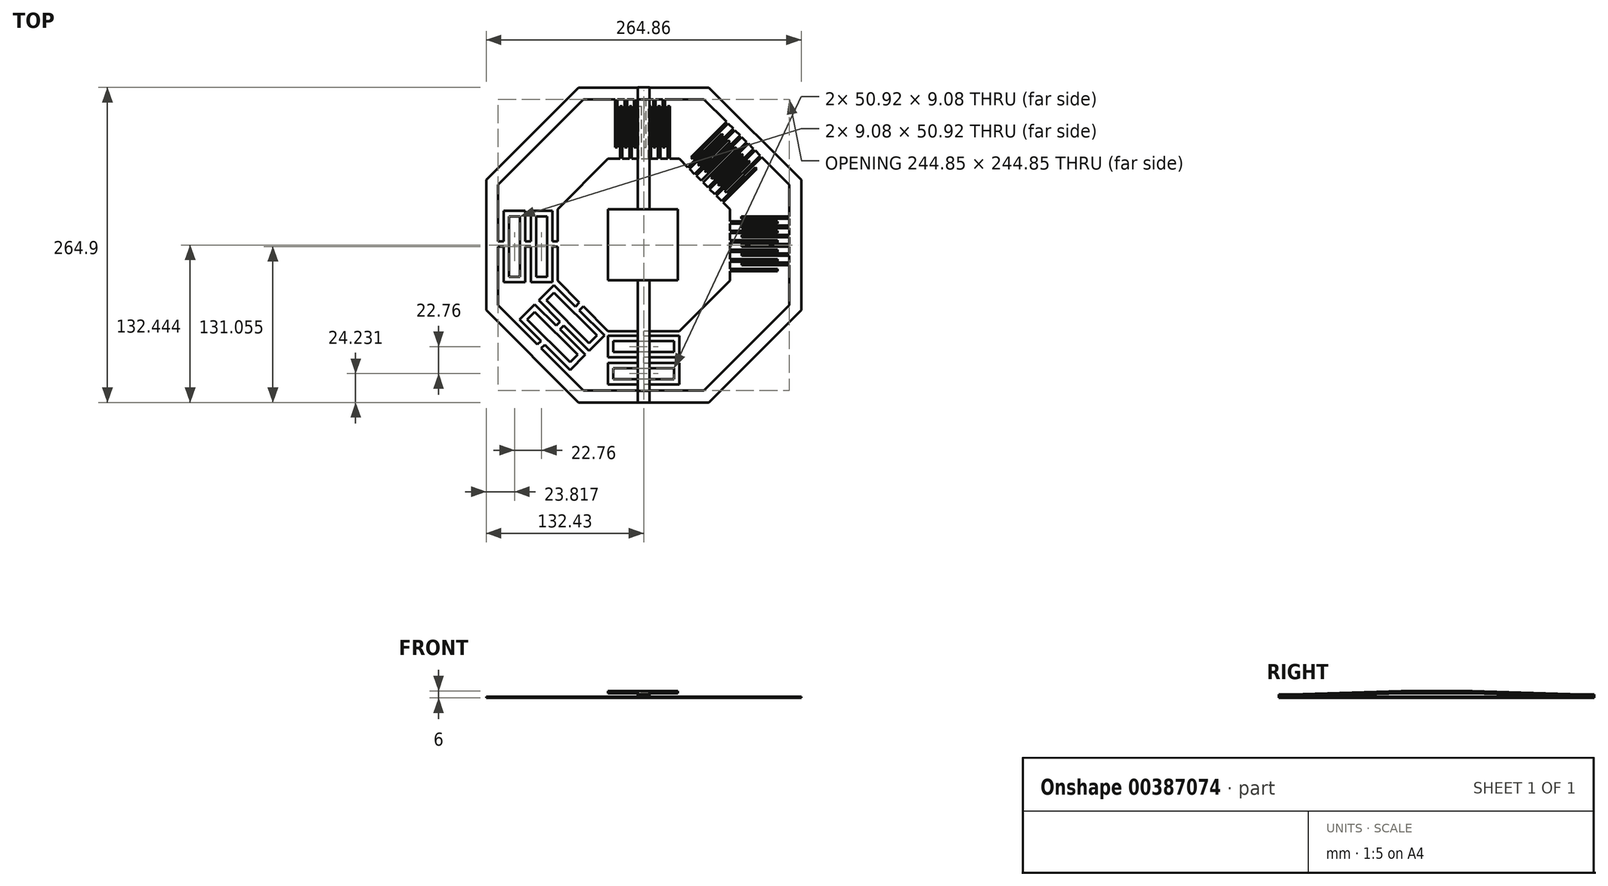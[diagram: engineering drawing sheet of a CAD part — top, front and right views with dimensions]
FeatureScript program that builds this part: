
annotation { "Feature Type Name" : "Feature", "Feature Type Description" : "" }
export const myFeature = defineFeature(function(context is Context, id is Id, definition is map)
    precondition{}
    {
        {
            var Q0;
            Q0=qCreatedBy(makeId("Top.planeOp"),FACE);
            var sketch = newSketch(context, id + "F0", { "sketchPlane" : qUnion([Q0])});
            skLineSegment(sketch, "E0", {"start": v(0, 0) * mm, "end": v(60, 0) * mm});
            skLineSegment(sketch, "E1", {"start": v(60, 0) * mm, "end": v(102.43, -42.43) * mm});
            skLineSegment(sketch, "E2", {"start": v(102.43, -42.43) * mm, "end": v(102.43, -52.43) * mm});
            skLineSegment(sketch, "E3", {"start": v(102.43, -102.43) * mm, "end": v(60, -144.85) * mm});
            skLineSegment(sketch, "E4", {"start": v(60, -144.85) * mm, "end": v(30, -144.85) * mm});
            skLineSegment(sketch, "E5", {"start": v(0, -144.85) * mm, "end": v(-20.84, -124.01) * mm});
            skLineSegment(sketch, "E6", {"start": v(-42.43, -102.43) * mm, "end": v(-42.43, -73.81) * mm});
            skLineSegment(sketch, "E7", {"start": v(-42.43, -42.43) * mm, "end": v(0, 0) * mm});
            skLineSegment(sketch, "E8.0", {"start": v(-92.43, -123.14) * mm, "end": v(-92.43, -73.81) * mm});
            skLineSegment(sketch, "E8.1", {"start": v(-20.71, -194.85) * mm, "end": v(-56.2, -159.37) * mm});
            skLineSegment(sketch, "E8.2", {"start": v(-92.43, -21.72) * mm, "end": v(-20.71, 50) * mm});
            skLineSegment(sketch, "E8.3", {"start": v(80.71, -194.85) * mm, "end": v(30, -194.85) * mm});
            skLineSegment(sketch, "E8.4", {"start": v(-20.71, 50) * mm, "end": v(6, 50) * mm});
            skLineSegment(sketch, "E8.6", {"start": v(152.43, -21.72) * mm, "end": v(152.43, -48.43) * mm});
            skLineSegment(sketch, "E8.7", {"start": v(152.43, -123.14) * mm, "end": v(80.71, -194.85) * mm});
            skLineSegment(sketch, "E9.0", {"start": v(-102.43, -17.57) * mm, "end": v(-24.85, 60) * mm});
            skLineSegment(sketch, "E9.1", {"start": v(-102.43, -127.28) * mm, "end": v(-102.43, -17.57) * mm});
            skLineSegment(sketch, "E9.2", {"start": v(-24.85, 60) * mm, "end": v(84.85, 60) * mm});
            skLineSegment(sketch, "E9.3", {"start": v(-24.85, -204.85) * mm, "end": v(-102.43, -127.28) * mm});
            skLineSegment(sketch, "E9.4", {"start": v(84.85, 60) * mm, "end": v(162.43, -17.57) * mm});
            skLineSegment(sketch, "E9.5", {"start": v(162.43, -17.57) * mm, "end": v(162.43, -127.28) * mm});
            skLineSegment(sketch, "E9.6", {"start": v(162.43, -127.28) * mm, "end": v(84.85, -204.85) * mm});
            skLineSegment(sketch, "E9.7", {"start": v(84.85, -204.85) * mm, "end": v(-24.85, -204.85) * mm});
            skLineSegment(sketch, "E10", {"start": v(10, 0) * mm, "end": v(10, 44.25) * mm});
            skLineSegment(sketch, "E11", {"start": v(10, 44.25) * mm, "end": v(12, 44.25) * mm});
            skLineSegment(sketch, "E12", {"start": v(12, 44.25) * mm, "end": v(12, 0) * mm});
            skLineSegment(sketch, "E13.1.0.0", {"start": v(20, 44.25) * mm, "end": v(20, 0) * mm});
            skLineSegment(sketch, "E13.1.0.1", {"start": v(18, 0) * mm, "end": v(18, 44.25) * mm});
            skLineSegment(sketch, "E13.1.0.2", {"start": v(18, 44.25) * mm, "end": v(20, 44.25) * mm});
            skLineSegment(sketch, "E13.2.0.0", {"start": v(28, 44.25) * mm, "end": v(28, 0) * mm});
            skLineSegment(sketch, "E13.2.0.1", {"start": v(26, 0) * mm, "end": v(26, 44.25) * mm});
            skLineSegment(sketch, "E13.2.0.2", {"start": v(26, 44.25) * mm, "end": v(28, 44.25) * mm});
            skLineSegment(sketch, "E13.3.0.0", {"start": v(36, 44.25) * mm, "end": v(36, 0) * mm});
            skLineSegment(sketch, "E13.3.0.1", {"start": v(34, 0) * mm, "end": v(34, 44.25) * mm});
            skLineSegment(sketch, "E13.3.0.2", {"start": v(34, 44.25) * mm, "end": v(36, 44.25) * mm});
            skLineSegment(sketch, "E13.4.0.0", {"start": v(44, 44.25) * mm, "end": v(44, 0) * mm});
            skLineSegment(sketch, "E13.4.0.1", {"start": v(42, 0) * mm, "end": v(42, 44.25) * mm});
            skLineSegment(sketch, "E13.4.0.2", {"start": v(42, 44.25) * mm, "end": v(44, 44.25) * mm});
            skLineSegment(sketch, "E13.5.0.0", {"start": v(52, 44.25) * mm, "end": v(52, 0) * mm});
            skLineSegment(sketch, "E13.5.0.1", {"start": v(50, 0) * mm, "end": v(50, 44.25) * mm});
            skLineSegment(sketch, "E13.5.0.2", {"start": v(50, 44.25) * mm, "end": v(52, 44.25) * mm});
            skLineSegment(sketch, "E13.direction1", {"start": v(10, 0) * mm, "end": v(18, 0) * mm, "construction": true});
            skLineSegment(sketch, "E14", {"start": v(102.43, -52.43) * mm, "end": v(142.43, -52.43) * mm});
            skLineSegment(sketch, "E15", {"start": v(142.43, -52.43) * mm, "end": v(142.43, -54.43) * mm});
            skLineSegment(sketch, "E16", {"start": v(142.43, -54.43) * mm, "end": v(102.43, -54.43) * mm});
            skLineSegment(sketch, "E17.1.0.0", {"start": v(102.43, -60.43) * mm, "end": v(142.43, -60.43) * mm});
            skLineSegment(sketch, "E17.1.0.1", {"start": v(142.43, -60.43) * mm, "end": v(142.43, -62.43) * mm});
            skLineSegment(sketch, "E17.1.0.2", {"start": v(142.43, -62.43) * mm, "end": v(102.43, -62.43) * mm});
            skLineSegment(sketch, "E17.2.0.0", {"start": v(102.43, -68.43) * mm, "end": v(142.43, -68.43) * mm});
            skLineSegment(sketch, "E17.2.0.1", {"start": v(142.43, -68.43) * mm, "end": v(142.43, -70.43) * mm});
            skLineSegment(sketch, "E17.2.0.2", {"start": v(142.43, -70.43) * mm, "end": v(102.43, -70.43) * mm});
            skLineSegment(sketch, "E17.3.0.0", {"start": v(102.43, -76.43) * mm, "end": v(142.43, -76.43) * mm});
            skLineSegment(sketch, "E17.3.0.1", {"start": v(142.43, -76.43) * mm, "end": v(142.43, -78.43) * mm});
            skLineSegment(sketch, "E17.3.0.2", {"start": v(142.43, -78.43) * mm, "end": v(102.43, -78.43) * mm});
            skLineSegment(sketch, "E17.4.0.0", {"start": v(102.43, -84.43) * mm, "end": v(142.43, -84.43) * mm});
            skLineSegment(sketch, "E17.4.0.1", {"start": v(142.43, -84.43) * mm, "end": v(142.43, -86.43) * mm});
            skLineSegment(sketch, "E17.4.0.2", {"start": v(142.43, -86.43) * mm, "end": v(102.43, -86.43) * mm});
            skLineSegment(sketch, "E17.5.0.0", {"start": v(102.43, -92.43) * mm, "end": v(142.43, -92.43) * mm});
            skLineSegment(sketch, "E17.5.0.1", {"start": v(142.43, -92.43) * mm, "end": v(142.43, -94.43) * mm});
            skLineSegment(sketch, "E17.5.0.2", {"start": v(142.43, -94.43) * mm, "end": v(102.43, -94.43) * mm});
            skLineSegment(sketch, "E17.direction1", {"start": v(102.43, -54.43) * mm, "end": v(102.43, -60.43) * mm, "construction": true});
            skLineSegment(sketch, "E18", {"start": v(80.71, 50) * mm, "end": v(99.6, 31.11) * mm});
            skLineSegment(sketch, "E19", {"start": v(67.07, -7.07) * mm, "end": v(95.36, 21.21) * mm});
            skLineSegment(sketch, "E20", {"start": v(95.36, 21.21) * mm, "end": v(96.77, 19.8) * mm});
            skLineSegment(sketch, "E21", {"start": v(96.77, 19.8) * mm, "end": v(68.49, -8.49) * mm});
            skLineSegment(sketch, "E22", {"start": v(68.49, -8.49) * mm, "end": v(67.07, -7.07) * mm});
            skLineSegment(sketch, "E23.1.0.0", {"start": v(72.73, -12.73) * mm, "end": v(101.01, 15.56) * mm});
            skLineSegment(sketch, "E23.1.0.1", {"start": v(102.43, 14.14) * mm, "end": v(74.14, -14.14) * mm});
            skLineSegment(sketch, "E23.1.0.2", {"start": v(101.01, 15.56) * mm, "end": v(102.43, 14.14) * mm});
            skLineSegment(sketch, "E23.1.0.3", {"start": v(74.14, -14.14) * mm, "end": v(72.73, -12.73) * mm});
            skLineSegment(sketch, "E23.2.0.0", {"start": v(78.38, -18.38) * mm, "end": v(106.67, 9.9) * mm});
            skLineSegment(sketch, "E23.2.0.1", {"start": v(108.08, 8.49) * mm, "end": v(79.8, -19.8) * mm});
            skLineSegment(sketch, "E23.2.0.2", {"start": v(106.67, 9.9) * mm, "end": v(108.08, 8.49) * mm});
            skLineSegment(sketch, "E23.2.0.3", {"start": v(79.8, -19.8) * mm, "end": v(78.38, -18.38) * mm});
            skLineSegment(sketch, "E23.3.0.0", {"start": v(84.04, -24.04) * mm, "end": v(112.33, 4.24) * mm});
            skLineSegment(sketch, "E23.3.0.1", {"start": v(113.74, 2.83) * mm, "end": v(85.46, -25.46) * mm});
            skLineSegment(sketch, "E23.3.0.2", {"start": v(112.33, 4.24) * mm, "end": v(113.74, 2.83) * mm});
            skLineSegment(sketch, "E23.3.0.3", {"start": v(85.46, -25.46) * mm, "end": v(84.04, -24.04) * mm});
            skLineSegment(sketch, "E23.4.0.0", {"start": v(89.7, -29.7) * mm, "end": v(117.98, -1.41) * mm});
            skLineSegment(sketch, "E23.4.0.1", {"start": v(119.4, -2.83) * mm, "end": v(91.11, -31.11) * mm});
            skLineSegment(sketch, "E23.4.0.2", {"start": v(117.98, -1.41) * mm, "end": v(119.4, -2.83) * mm});
            skLineSegment(sketch, "E23.4.0.3", {"start": v(91.11, -31.11) * mm, "end": v(89.7, -29.7) * mm});
            skLineSegment(sketch, "E23.5.0.0", {"start": v(95.36, -35.36) * mm, "end": v(123.64, -7.07) * mm});
            skLineSegment(sketch, "E23.5.0.1", {"start": v(125.05, -8.49) * mm, "end": v(96.77, -36.77) * mm});
            skLineSegment(sketch, "E23.5.0.2", {"start": v(123.64, -7.07) * mm, "end": v(125.05, -8.49) * mm});
            skLineSegment(sketch, "E23.5.0.3", {"start": v(96.77, -36.77) * mm, "end": v(95.36, -35.36) * mm});
            skLineSegment(sketch, "E23.direction1", {"start": v(68.49, -8.49) * mm, "end": v(74.14, -14.14) * mm, "construction": true});
            skLineSegment(sketch, "E24", {"start": v(-87.7, -43.81) * mm, "end": v(-69.53, -43.81) * mm});
            skLineSegment(sketch, "E25", {"start": v(-69.53, -43.81) * mm, "end": v(-69.53, -69.27) * mm});
            skLineSegment(sketch, "E26", {"start": v(-69.53, -103.81) * mm, "end": v(-87.7, -103.81) * mm});
            skLineSegment(sketch, "E27", {"start": v(-87.7, -103.81) * mm, "end": v(-87.7, -73.81) * mm});
            skLineSegment(sketch, "E28.0", {"start": v(-83.15, -48.35) * mm, "end": v(-74.07, -48.35) * mm});
            skLineSegment(sketch, "E28.1", {"start": v(-83.15, -99.27) * mm, "end": v(-83.15, -48.35) * mm});
            skLineSegment(sketch, "E28.2", {"start": v(-74.07, -99.27) * mm, "end": v(-83.15, -99.27) * mm});
            skLineSegment(sketch, "E28.3", {"start": v(-74.07, -48.35) * mm, "end": v(-74.07, -99.27) * mm});
            skLineSegment(sketch, "E29", {"start": v(-64.93, -43.81) * mm, "end": v(-46.77, -43.81) * mm});
            skLineSegment(sketch, "E30", {"start": v(-46.77, -43.81) * mm, "end": v(-46.77, -69.27) * mm});
            skLineSegment(sketch, "E31", {"start": v(-46.77, -103.81) * mm, "end": v(-64.93, -103.81) * mm});
            skLineSegment(sketch, "E32", {"start": v(-64.93, -103.81) * mm, "end": v(-64.93, -73.81) * mm});
            skLineSegment(sketch, "E33.0", {"start": v(-60.4, -48.35) * mm, "end": v(-51.31, -48.35) * mm});
            skLineSegment(sketch, "E33.1", {"start": v(-60.4, -99.27) * mm, "end": v(-60.4, -48.35) * mm});
            skLineSegment(sketch, "E33.2", {"start": v(-51.31, -99.27) * mm, "end": v(-60.4, -99.27) * mm});
            skLineSegment(sketch, "E33.3", {"start": v(-51.31, -48.35) * mm, "end": v(-51.31, -99.27) * mm});
            skLineSegment(sketch, "E34", {"start": v(-69.53, -73.81) * mm, "end": v(-64.93, -73.81) * mm});
            skLineSegment(sketch, "E35", {"start": v(-69.53, -69.27) * mm, "end": v(-64.93, -69.27) * mm});
            skLineSegment(sketch, "E36.trimOffspring", {"start": v(-46.77, -73.81) * mm, "end": v(-46.77, -103.81) * mm});
            skLineSegment(sketch, "E37.trimOffspring", {"start": v(-69.53, -73.81) * mm, "end": v(-69.53, -103.81) * mm});
            skLineSegment(sketch, "E38.trimOffspring", {"start": v(-64.93, -69.27) * mm, "end": v(-64.93, -43.81) * mm});
            skLineSegment(sketch, "E39.trimOffspring", {"start": v(-87.7, -69.27) * mm, "end": v(-87.7, -43.81) * mm});
            skLineSegment(sketch, "E40", {"start": v(-87.7, -69.27) * mm, "end": v(-92.43, -69.27) * mm});
            skLineSegment(sketch, "E41", {"start": v(-87.7, -73.81) * mm, "end": v(-92.43, -73.81) * mm});
            skLineSegment(sketch, "E42", {"start": v(-46.77, -69.27) * mm, "end": v(-42.43, -69.27) * mm});
            skLineSegment(sketch, "E43", {"start": v(-46.77, -73.81) * mm, "end": v(-42.43, -73.81) * mm});
            skLineSegment(sketch, "E44.trimOffspring", {"start": v(-42.43, -69.27) * mm, "end": v(-42.43, -42.43) * mm});
            skLineSegment(sketch, "E45.trimOffspring", {"start": v(-92.43, -69.27) * mm, "end": v(-92.43, -21.72) * mm});
            skLineSegment(sketch, "E46", {"start": v(0, -189.72) * mm, "end": v(0, -171.56) * mm});
            skLineSegment(sketch, "E47", {"start": v(0, -171.56) * mm, "end": v(25.46, -171.56) * mm});
            skLineSegment(sketch, "E48", {"start": v(60, -171.56) * mm, "end": v(60, -189.72) * mm});
            skLineSegment(sketch, "E49", {"start": v(60, -189.72) * mm, "end": v(30, -189.72) * mm});
            skLineSegment(sketch, "E50.0", {"start": v(4.54, -185.18) * mm, "end": v(4.54, -176.1) * mm});
            skLineSegment(sketch, "E50.1", {"start": v(55.46, -185.18) * mm, "end": v(4.54, -185.18) * mm});
            skLineSegment(sketch, "E50.2", {"start": v(55.46, -176.1) * mm, "end": v(55.46, -185.18) * mm});
            skLineSegment(sketch, "E50.3", {"start": v(4.54, -176.1) * mm, "end": v(55.46, -176.1) * mm});
            skLineSegment(sketch, "E51", {"start": v(0, -166.96) * mm, "end": v(0, -148.8) * mm});
            skLineSegment(sketch, "E52", {"start": v(0, -148.8) * mm, "end": v(25.46, -148.8) * mm});
            skLineSegment(sketch, "E53", {"start": v(60, -148.8) * mm, "end": v(60, -166.96) * mm});
            skLineSegment(sketch, "E54", {"start": v(60, -166.96) * mm, "end": v(30, -166.96) * mm});
            skLineSegment(sketch, "E55.0", {"start": v(4.54, -162.42) * mm, "end": v(4.54, -153.34) * mm});
            skLineSegment(sketch, "E55.1", {"start": v(55.46, -162.42) * mm, "end": v(4.54, -162.42) * mm});
            skLineSegment(sketch, "E55.2", {"start": v(55.46, -153.34) * mm, "end": v(55.46, -162.42) * mm});
            skLineSegment(sketch, "E55.3", {"start": v(4.54, -153.34) * mm, "end": v(55.46, -153.34) * mm});
            skLineSegment(sketch, "E56", {"start": v(30, -171.56) * mm, "end": v(30, -166.96) * mm});
            skLineSegment(sketch, "E57", {"start": v(25.46, -171.56) * mm, "end": v(25.46, -166.96) * mm});
            skLineSegment(sketch, "E58.trimOffspring", {"start": v(30, -148.8) * mm, "end": v(60, -148.8) * mm});
            skLineSegment(sketch, "E59.trimOffspring", {"start": v(30, -171.56) * mm, "end": v(60, -171.56) * mm});
            skLineSegment(sketch, "E60.trimOffspring", {"start": v(25.46, -166.96) * mm, "end": v(0, -166.96) * mm});
            skLineSegment(sketch, "E61.trimOffspring", {"start": v(25.46, -189.72) * mm, "end": v(0, -189.72) * mm});
            skLineSegment(sketch, "E62", {"start": v(25.46, -148.8) * mm, "end": v(25.46, -144.85) * mm});
            skLineSegment(sketch, "E63", {"start": v(30, -148.8) * mm, "end": v(30, -144.85) * mm});
            skLineSegment(sketch, "E64", {"start": v(25.46, -189.72) * mm, "end": v(25.46, -194.85) * mm});
            skLineSegment(sketch, "E65", {"start": v(30, -189.72) * mm, "end": v(30, -194.85) * mm});
            skLineSegment(sketch, "E66.trimOffspring", {"start": v(25.46, -144.85) * mm, "end": v(0, -144.85) * mm});
            skLineSegment(sketch, "E67.trimOffspring", {"start": v(25.46, -194.85) * mm, "end": v(-20.71, -194.85) * mm});
            skLineSegment(sketch, "E68", {"start": v(-74.34, -135.09) * mm, "end": v(-61.5, -122.25) * mm});
            skLineSegment(sketch, "E69", {"start": v(-61.5, -122.25) * mm, "end": v(-43.5, -140.25) * mm});
            skLineSegment(sketch, "E70", {"start": v(-19.07, -164.67) * mm, "end": v(-31.91, -177.51) * mm});
            skLineSegment(sketch, "E71", {"start": v(-31.91, -177.51) * mm, "end": v(-53.13, -156.3) * mm});
            skLineSegment(sketch, "E72.0", {"start": v(-67.92, -135.09) * mm, "end": v(-61.5, -128.67) * mm});
            skLineSegment(sketch, "E72.1", {"start": v(-31.91, -171.1) * mm, "end": v(-67.92, -135.09) * mm});
            skLineSegment(sketch, "E72.2", {"start": v(-25.5, -164.67) * mm, "end": v(-31.91, -171.1) * mm});
            skLineSegment(sketch, "E72.3", {"start": v(-61.5, -128.67) * mm, "end": v(-25.5, -164.67) * mm});
            skLineSegment(sketch, "E73", {"start": v(-58.25, -119) * mm, "end": v(-45.4, -106.15) * mm});
            skLineSegment(sketch, "E74", {"start": v(-45.4, -106.15) * mm, "end": v(-27.4, -124.15) * mm});
            skLineSegment(sketch, "E75", {"start": v(-2.98, -148.58) * mm, "end": v(-15.82, -161.42) * mm});
            skLineSegment(sketch, "E76", {"start": v(-15.82, -161.42) * mm, "end": v(-37.03, -140.2) * mm});
            skLineSegment(sketch, "E77.0", {"start": v(-51.83, -119) * mm, "end": v(-45.4, -112.57) * mm});
            skLineSegment(sketch, "E77.1", {"start": v(-15.82, -155) * mm, "end": v(-51.83, -119) * mm});
            skLineSegment(sketch, "E77.2", {"start": v(-9.4, -148.58) * mm, "end": v(-15.82, -155) * mm});
            skLineSegment(sketch, "E77.3", {"start": v(-45.4, -112.57) * mm, "end": v(-9.4, -148.58) * mm});
            skLineSegment(sketch, "E78", {"start": v(-40.29, -143.46) * mm, "end": v(-37.03, -140.2) * mm});
            skLineSegment(sketch, "E79", {"start": v(-43.5, -140.25) * mm, "end": v(-40.24, -137) * mm});
            skLineSegment(sketch, "E80.trimOffspring", {"start": v(-24.2, -127.36) * mm, "end": v(-2.98, -148.58) * mm});
            skLineSegment(sketch, "E81.trimOffspring", {"start": v(-40.29, -143.46) * mm, "end": v(-19.07, -164.67) * mm});
            skLineSegment(sketch, "E82.trimOffspring", {"start": v(-40.24, -137) * mm, "end": v(-58.25, -119) * mm});
            skLineSegment(sketch, "E83.trimOffspring", {"start": v(-56.34, -153.09) * mm, "end": v(-74.34, -135.09) * mm});
            skLineSegment(sketch, "E84", {"start": v(-27.4, -124.15) * mm, "end": v(-24.05, -120.8) * mm});
            skLineSegment(sketch, "E85", {"start": v(-24.2, -127.36) * mm, "end": v(-20.84, -124.01) * mm});
            skLineSegment(sketch, "E86", {"start": v(-56.34, -153.09) * mm, "end": v(-59.4, -156.16) * mm});
            skLineSegment(sketch, "E87", {"start": v(-53.13, -156.3) * mm, "end": v(-56.2, -159.37) * mm});
            skLineSegment(sketch, "E88.trimOffspring", {"start": v(-24.05, -120.8) * mm, "end": v(-42.43, -102.43) * mm});
            skLineSegment(sketch, "E89.trimOffspring", {"start": v(-59.4, -156.16) * mm, "end": v(-92.43, -123.14) * mm});
            skLineSegment(sketch, "E90", {"start": v(6, 50) * mm, "end": v(6, 9.64) * mm});
            skLineSegment(sketch, "E91", {"start": v(6, 9.64) * mm, "end": v(8, 9.64) * mm});
            skLineSegment(sketch, "E92", {"start": v(8, 9.64) * mm, "end": v(8, 50) * mm});
            skLineSegment(sketch, "E93", {"start": v(99.6, 31.11) * mm, "end": v(69.79, 1.3) * mm});
            skLineSegment(sketch, "E94", {"start": v(69.79, 1.3) * mm, "end": v(71.2, -0.1) * mm});
            skLineSegment(sketch, "E95", {"start": v(71.2, -0.1) * mm, "end": v(101.01, 29.7) * mm});
            skLineSegment(sketch, "E96.1.0.0", {"start": v(105.26, 25.46) * mm, "end": v(75.45, -4.35) * mm});
            skLineSegment(sketch, "E96.1.0.1", {"start": v(75.45, -4.35) * mm, "end": v(76.86, -5.76) * mm});
            skLineSegment(sketch, "E96.1.0.2", {"start": v(76.86, -5.76) * mm, "end": v(106.67, 24.05) * mm});
            skLineSegment(sketch, "E96.2.0.0", {"start": v(110.92, 19.8) * mm, "end": v(81.1, -10) * mm});
            skLineSegment(sketch, "E96.2.0.1", {"start": v(81.1, -10) * mm, "end": v(82.52, -11.42) * mm});
            skLineSegment(sketch, "E96.2.0.2", {"start": v(82.52, -11.42) * mm, "end": v(112.33, 18.4) * mm});
            skLineSegment(sketch, "E96.3.0.0", {"start": v(116.58, 14.15) * mm, "end": v(86.77, -15.66) * mm});
            skLineSegment(sketch, "E96.3.0.1", {"start": v(86.77, -15.66) * mm, "end": v(88.18, -17.07) * mm});
            skLineSegment(sketch, "E96.3.0.2", {"start": v(88.18, -17.07) * mm, "end": v(118, 12.74) * mm});
            skLineSegment(sketch, "E96.4.0.0", {"start": v(122.24, 8.5) * mm, "end": v(92.43, -21.31) * mm});
            skLineSegment(sketch, "E96.4.0.1", {"start": v(92.43, -21.31) * mm, "end": v(93.84, -22.73) * mm});
            skLineSegment(sketch, "E96.4.0.2", {"start": v(93.84, -22.73) * mm, "end": v(123.65, 7.08) * mm});
            skLineSegment(sketch, "E96.5.0.0", {"start": v(127.9, 2.84) * mm, "end": v(98.09, -26.96) * mm});
            skLineSegment(sketch, "E96.5.0.1", {"start": v(98.09, -26.96) * mm, "end": v(99.5, -28.38) * mm});
            skLineSegment(sketch, "E96.5.0.2", {"start": v(99.5, -28.38) * mm, "end": v(129.31, 1.43) * mm});
            skLineSegment(sketch, "E97.1.0.0", {"start": v(14, 50) * mm, "end": v(14, 9.64) * mm});
            skLineSegment(sketch, "E97.1.0.1", {"start": v(14, 9.64) * mm, "end": v(16, 9.64) * mm});
            skLineSegment(sketch, "E97.1.0.2", {"start": v(16, 9.64) * mm, "end": v(16, 50) * mm});
            skLineSegment(sketch, "E97.2.0.0", {"start": v(22, 50) * mm, "end": v(22, 9.64) * mm});
            skLineSegment(sketch, "E97.2.0.1", {"start": v(22, 9.64) * mm, "end": v(24, 9.64) * mm});
            skLineSegment(sketch, "E97.2.0.2", {"start": v(24, 9.64) * mm, "end": v(24, 50) * mm});
            skLineSegment(sketch, "E97.3.0.0", {"start": v(30, 50) * mm, "end": v(30, 9.64) * mm});
            skLineSegment(sketch, "E97.3.0.1", {"start": v(30, 9.64) * mm, "end": v(32, 9.64) * mm});
            skLineSegment(sketch, "E97.3.0.2", {"start": v(32, 9.64) * mm, "end": v(32, 50) * mm});
            skLineSegment(sketch, "E97.4.0.0", {"start": v(38, 50) * mm, "end": v(38, 9.64) * mm});
            skLineSegment(sketch, "E97.4.0.1", {"start": v(38, 9.64) * mm, "end": v(40, 9.64) * mm});
            skLineSegment(sketch, "E97.4.0.2", {"start": v(40, 9.64) * mm, "end": v(40, 50) * mm});
            skLineSegment(sketch, "E97.5.0.0", {"start": v(46, 50) * mm, "end": v(46, 9.64) * mm});
            skLineSegment(sketch, "E97.5.0.1", {"start": v(46, 9.64) * mm, "end": v(48, 9.64) * mm});
            skLineSegment(sketch, "E97.5.0.2", {"start": v(48, 9.64) * mm, "end": v(48, 50) * mm});
            skLineSegment(sketch, "E98.trimOffspring", {"start": v(129.3, 1.41) * mm, "end": v(152.43, -21.72) * mm});
            skLineSegment(sketch, "E99.trimOffspring", {"start": v(123.64, 7.07) * mm, "end": v(127.88, 2.83) * mm});
            skLineSegment(sketch, "E100.trimOffspring", {"start": v(117.98, 12.73) * mm, "end": v(122.22, 8.49) * mm});
            skLineSegment(sketch, "E101.trimOffspring", {"start": v(112.33, 18.39) * mm, "end": v(116.57, 14.14) * mm});
            skLineSegment(sketch, "E102.trimOffspring", {"start": v(106.67, 24.04) * mm, "end": v(110.91, 19.8) * mm});
            skLineSegment(sketch, "E103.trimOffspring", {"start": v(101.01, 29.7) * mm, "end": v(105.25, 25.46) * mm});
            skLineSegment(sketch, "E104.trimOffspring", {"start": v(48, 50) * mm, "end": v(80.71, 50) * mm});
            skLineSegment(sketch, "E105.trimOffspring", {"start": v(40, 50) * mm, "end": v(46, 50) * mm});
            skLineSegment(sketch, "E106.trimOffspring", {"start": v(32, 50) * mm, "end": v(38, 50) * mm});
            skLineSegment(sketch, "E107.trimOffspring", {"start": v(24, 50) * mm, "end": v(30, 50) * mm});
            skLineSegment(sketch, "E108.trimOffspring", {"start": v(16, 50) * mm, "end": v(22, 50) * mm});
            skLineSegment(sketch, "E109.trimOffspring", {"start": v(8, 50) * mm, "end": v(14, 50) * mm});
            skLineSegment(sketch, "E110", {"start": v(152.43, -48.43) * mm, "end": v(112.16, -48.43) * mm});
            skLineSegment(sketch, "E111", {"start": v(112.16, -48.43) * mm, "end": v(112.16, -50.43) * mm});
            skLineSegment(sketch, "E112", {"start": v(112.16, -50.43) * mm, "end": v(152.43, -50.43) * mm});
            skLineSegment(sketch, "E113.1.0.0", {"start": v(152.43, -56.2) * mm, "end": v(112.2, -56.2) * mm});
            skLineSegment(sketch, "E113.1.0.1", {"start": v(112.2, -56.2) * mm, "end": v(112.2, -58.2) * mm});
            skLineSegment(sketch, "E113.1.0.2", {"start": v(112.2, -58.2) * mm, "end": v(152.43, -58.2) * mm});
            skLineSegment(sketch, "E113.2.0.0", {"start": v(152.43, -63.97) * mm, "end": v(112.24, -63.97) * mm});
            skLineSegment(sketch, "E113.2.0.1", {"start": v(112.24, -63.97) * mm, "end": v(112.24, -65.97) * mm});
            skLineSegment(sketch, "E113.2.0.2", {"start": v(112.24, -65.97) * mm, "end": v(152.43, -65.97) * mm});
            skLineSegment(sketch, "E113.3.0.0", {"start": v(152.43, -71.75) * mm, "end": v(112.29, -71.75) * mm});
            skLineSegment(sketch, "E113.3.0.1", {"start": v(112.29, -71.75) * mm, "end": v(112.29, -73.75) * mm});
            skLineSegment(sketch, "E113.3.0.2", {"start": v(112.29, -73.75) * mm, "end": v(152.43, -73.75) * mm});
            skLineSegment(sketch, "E113.4.0.0", {"start": v(152.43, -79.52) * mm, "end": v(112.33, -79.52) * mm});
            skLineSegment(sketch, "E113.4.0.1", {"start": v(112.33, -79.52) * mm, "end": v(112.33, -81.52) * mm});
            skLineSegment(sketch, "E113.4.0.2", {"start": v(112.33, -81.52) * mm, "end": v(152.43, -81.52) * mm});
            skLineSegment(sketch, "E113.5.0.0", {"start": v(152.43, -87.3) * mm, "end": v(112.38, -87.3) * mm});
            skLineSegment(sketch, "E113.5.0.1", {"start": v(112.38, -87.3) * mm, "end": v(112.38, -89.3) * mm});
            skLineSegment(sketch, "E113.5.0.2", {"start": v(112.38, -89.3) * mm, "end": v(152.43, -89.3) * mm});
            skLineSegment(sketch, "E114.trimOffspring", {"start": v(152.43, -58.2) * mm, "end": v(152.43, -63.97) * mm});
            skLineSegment(sketch, "E115.trimOffspring", {"start": v(152.43, -50.43) * mm, "end": v(152.43, -56.2) * mm});
            skLineSegment(sketch, "E116.trimOffspring", {"start": v(152.43, -65.97) * mm, "end": v(152.43, -71.75) * mm});
            skLineSegment(sketch, "E117.trimOffspring", {"start": v(152.43, -73.75) * mm, "end": v(152.43, -79.52) * mm});
            skLineSegment(sketch, "E118.trimOffspring", {"start": v(152.43, -81.52) * mm, "end": v(152.43, -87.3) * mm});
            skLineSegment(sketch, "E119.trimOffspring", {"start": v(152.43, -89.3) * mm, "end": v(152.43, -123.14) * mm});
            skLineSegment(sketch, "E120.trimOffspring", {"start": v(102.43, -94.43) * mm, "end": v(102.43, -102.43) * mm});
            skLineSegment(sketch, "E121.trimOffspring", {"start": v(102.43, -86.43) * mm, "end": v(102.43, -92.43) * mm});
            skLineSegment(sketch, "E122.trimOffspring", {"start": v(102.43, -78.43) * mm, "end": v(102.43, -84.43) * mm});
            skLineSegment(sketch, "E123.trimOffspring", {"start": v(102.43, -62.43) * mm, "end": v(102.43, -76.43) * mm});
            skLineSegment(sketch, "E124.trimOffspring", {"start": v(102.43, -54.43) * mm, "end": v(102.43, -60.43) * mm});
            skSolve(sketch);
        }
        {
            var Q0;
            {var subQ36=sQuery(id+"F0.wireOp",EDGE,"E3");Q0=makeQuery(id+"F0.imprint","IMPRINT",FACE,{"disambiguationData":[TD([[makeQuery(id+"F0.imprint","IMPRINT",EDGE,{"derivedFrom":subQ36}),-1.0]])]});}
            var Q1;
            {var subQ0=sQuery(id+"F0.wireOp",EDGE,"E17.5.0.0");Q1=makeQuery(id+"F0.imprint","IMPRINT",FACE,{"disambiguationData":[TD([[makeQuery(id+"F0.imprint","IMPRINT",EDGE,{"derivedFrom":subQ0}),-1.0]])]});}
            var Q2;
            {var subQ0=sQuery(id+"F0.wireOp",EDGE,"E17.4.0.0");Q2=makeQuery(id+"F0.imprint","IMPRINT",FACE,{"disambiguationData":[TD([[makeQuery(id+"F0.imprint","IMPRINT",EDGE,{"derivedFrom":subQ0}),-1.0]])]});}
            var Q3;
            {var subQ0=sQuery(id+"F0.wireOp",EDGE,"E17.3.0.0");Q3=makeQuery(id+"F0.imprint","IMPRINT",FACE,{"disambiguationData":[TD([[makeQuery(id+"F0.imprint","IMPRINT",EDGE,{"derivedFrom":subQ0}),-1.0]])]});}
            var Q4;
            {var subQ0=sQuery(id+"F0.wireOp",EDGE,"E17.2.0.0");Q4=makeQuery(id+"F0.imprint","IMPRINT",FACE,{"disambiguationData":[TD([[makeQuery(id+"F0.imprint","IMPRINT",EDGE,{"derivedFrom":subQ0}),-1.0]])]});}
            var Q5;
            {var subQ0=sQuery(id+"F0.wireOp",EDGE,"E17.1.0.0");Q5=makeQuery(id+"F0.imprint","IMPRINT",FACE,{"disambiguationData":[TD([[makeQuery(id+"F0.imprint","IMPRINT",EDGE,{"derivedFrom":subQ0}),-1.0]])]});}
            var Q6;
            {var subQ0=sQuery(id+"F0.wireOp",EDGE,"E14");Q6=makeQuery(id+"F0.imprint","IMPRINT",FACE,{"disambiguationData":[TD([[makeQuery(id+"F0.imprint","IMPRINT",EDGE,{"derivedFrom":subQ0}),-1.0]])]});}
            var Q7;
            Q7=makeQuery(id+"F0.imprint","IMPRINT",FACE,{"disambiguationData":[TD([[makeQuery(id+"F0.imprint","IMPRINT",EDGE,{"derivedFrom":sQuery(id+"F0.wireOp",EDGE,"E23.5.0.0")}),-1.0]])]});
            var Q8;
            Q8=makeQuery(id+"F0.imprint","IMPRINT",FACE,{"disambiguationData":[TD([[makeQuery(id+"F0.imprint","IMPRINT",EDGE,{"derivedFrom":sQuery(id+"F0.wireOp",EDGE,"E23.4.0.0")}),-1.0]])]});
            var Q9;
            Q9=makeQuery(id+"F0.imprint","IMPRINT",FACE,{"disambiguationData":[TD([[makeQuery(id+"F0.imprint","IMPRINT",EDGE,{"derivedFrom":sQuery(id+"F0.wireOp",EDGE,"E23.3.0.0")}),-1.0]])]});
            var Q10;
            Q10=makeQuery(id+"F0.imprint","IMPRINT",FACE,{"disambiguationData":[TD([[makeQuery(id+"F0.imprint","IMPRINT",EDGE,{"derivedFrom":sQuery(id+"F0.wireOp",EDGE,"E23.2.0.0")}),-1.0]])]});
            var Q11;
            Q11=makeQuery(id+"F0.imprint","IMPRINT",FACE,{"disambiguationData":[TD([[makeQuery(id+"F0.imprint","IMPRINT",EDGE,{"derivedFrom":sQuery(id+"F0.wireOp",EDGE,"E23.1.0.0")}),-1.0]])]});
            var Q12;
            Q12=makeQuery(id+"F0.imprint","IMPRINT",FACE,{"disambiguationData":[TD([[makeQuery(id+"F0.imprint","IMPRINT",EDGE,{"derivedFrom":sQuery(id+"F0.wireOp",EDGE,"E19")}),-1.0]])]});
            var Q13;
            {var subQ0=sQuery(id+"F0.wireOp",EDGE,"E13.5.0.0");Q13=makeQuery(id+"F0.imprint","IMPRINT",FACE,{"disambiguationData":[TD([[makeQuery(id+"F0.imprint","IMPRINT",EDGE,{"derivedFrom":subQ0}),-1.0]])]});}
            var Q14;
            {var subQ0=sQuery(id+"F0.wireOp",EDGE,"E13.4.0.0");Q14=makeQuery(id+"F0.imprint","IMPRINT",FACE,{"disambiguationData":[TD([[makeQuery(id+"F0.imprint","IMPRINT",EDGE,{"derivedFrom":subQ0}),-1.0]])]});}
            var Q15;
            {var subQ0=sQuery(id+"F0.wireOp",EDGE,"E13.3.0.0");Q15=makeQuery(id+"F0.imprint","IMPRINT",FACE,{"disambiguationData":[TD([[makeQuery(id+"F0.imprint","IMPRINT",EDGE,{"derivedFrom":subQ0}),-1.0]])]});}
            var Q16;
            {var subQ0=sQuery(id+"F0.wireOp",EDGE,"E13.2.0.0");Q16=makeQuery(id+"F0.imprint","IMPRINT",FACE,{"disambiguationData":[TD([[makeQuery(id+"F0.imprint","IMPRINT",EDGE,{"derivedFrom":subQ0}),-1.0]])]});}
            var Q17;
            {var subQ0=sQuery(id+"F0.wireOp",EDGE,"E13.1.0.0");Q17=makeQuery(id+"F0.imprint","IMPRINT",FACE,{"disambiguationData":[TD([[makeQuery(id+"F0.imprint","IMPRINT",EDGE,{"derivedFrom":subQ0}),-1.0]])]});}
            var Q18;
            {var subQ0=sQuery(id+"F0.wireOp",EDGE,"E10");Q18=makeQuery(id+"F0.imprint","IMPRINT",FACE,{"disambiguationData":[TD([[makeQuery(id+"F0.imprint","IMPRINT",EDGE,{"derivedFrom":subQ0}),-1.0]])]});}
            extrude(context, id + "F1", {"entities" : qUnion([Q0, Q1, Q2, Q3, Q4, Q5, Q6, Q7, Q8, Q9, Q10, Q11, Q12, Q13, Q14, Q15, Q16, Q17, Q18]), "depth" : 1 * mm});
        }
        {
            var Q0;
            Q0=makeQuery(id+"F1.opExtrude","CAP_FACE",FACE,{"disambiguationData":[OSD([sQuery(id+"F0.wireOp",EDGE,"E0"),sQuery(id+"F0.wireOp",EDGE,"E1"),sQuery(id+"F0.wireOp",EDGE,"E2"),sQuery(id+"F0.wireOp",EDGE,"E3"),sQuery(id+"F0.wireOp",EDGE,"E4"),sQuery(id+"F0.wireOp",EDGE,"E5"),sQuery(id+"F0.wireOp",EDGE,"E6"),sQuery(id+"F0.wireOp",EDGE,"E7"),sQuery(id+"F0.wireOp",EDGE,"E8.0"),sQuery(id+"F0.wireOp",EDGE,"E8.1"),sQuery(id+"F0.wireOp",EDGE,"E8.2"),sQuery(id+"F0.wireOp",EDGE,"E8.3"),sQuery(id+"F0.wireOp",EDGE,"E8.4"),sQuery(id+"F0.wireOp",EDGE,"E8.6"),sQuery(id+"F0.wireOp",EDGE,"E8.7"),sQuery(id+"F0.wireOp",EDGE,"E9.0"),sQuery(id+"F0.wireOp",EDGE,"E9.1"),sQuery(id+"F0.wireOp",EDGE,"E9.2"),sQuery(id+"F0.wireOp",EDGE,"E9.3"),sQuery(id+"F0.wireOp",EDGE,"E9.4"),sQuery(id+"F0.wireOp",EDGE,"E9.5"),sQuery(id+"F0.wireOp",EDGE,"E9.6"),sQuery(id+"F0.wireOp",EDGE,"E9.7"),sQuery(id+"F0.wireOp",EDGE,"E10"),sQuery(id+"F0.wireOp",EDGE,"E11"),sQuery(id+"F0.wireOp",EDGE,"E12"),sQuery(id+"F0.wireOp",EDGE,"E13.1.0.0"),sQuery(id+"F0.wireOp",EDGE,"E13.1.0.1"),sQuery(id+"F0.wireOp",EDGE,"E13.1.0.2"),sQuery(id+"F0.wireOp",EDGE,"E13.2.0.0"),sQuery(id+"F0.wireOp",EDGE,"E13.2.0.1"),sQuery(id+"F0.wireOp",EDGE,"E13.2.0.2"),sQuery(id+"F0.wireOp",EDGE,"E13.3.0.0"),sQuery(id+"F0.wireOp",EDGE,"E13.3.0.1"),sQuery(id+"F0.wireOp",EDGE,"E13.3.0.2"),sQuery(id+"F0.wireOp",EDGE,"E13.4.0.0"),sQuery(id+"F0.wireOp",EDGE,"E13.4.0.1"),sQuery(id+"F0.wireOp",EDGE,"E13.4.0.2"),sQuery(id+"F0.wireOp",EDGE,"E13.5.0.0"),sQuery(id+"F0.wireOp",EDGE,"E13.5.0.1"),sQuery(id+"F0.wireOp",EDGE,"E13.5.0.2"),sQuery(id+"F0.wireOp",EDGE,"E14"),sQuery(id+"F0.wireOp",EDGE,"E15"),sQuery(id+"F0.wireOp",EDGE,"E16"),sQuery(id+"F0.wireOp",EDGE,"E17.1.0.0"),sQuery(id+"F0.wireOp",EDGE,"E17.1.0.1"),sQuery(id+"F0.wireOp",EDGE,"E17.1.0.2"),sQuery(id+"F0.wireOp",EDGE,"E17.2.0.0"),sQuery(id+"F0.wireOp",EDGE,"E17.2.0.1"),sQuery(id+"F0.wireOp",EDGE,"E17.2.0.2"),sQuery(id+"F0.wireOp",EDGE,"E17.3.0.0"),sQuery(id+"F0.wireOp",EDGE,"E17.3.0.1"),sQuery(id+"F0.wireOp",EDGE,"E17.3.0.2"),sQuery(id+"F0.wireOp",EDGE,"E17.4.0.0"),sQuery(id+"F0.wireOp",EDGE,"E17.4.0.1"),sQuery(id+"F0.wireOp",EDGE,"E17.4.0.2"),sQuery(id+"F0.wireOp",EDGE,"E17.5.0.0"),sQuery(id+"F0.wireOp",EDGE,"E17.5.0.1"),sQuery(id+"F0.wireOp",EDGE,"E17.5.0.2"),sQuery(id+"F0.wireOp",EDGE,"E18"),sQuery(id+"F0.wireOp",EDGE,"E19"),sQuery(id+"F0.wireOp",EDGE,"E20"),sQuery(id+"F0.wireOp",EDGE,"E21"),sQuery(id+"F0.wireOp",EDGE,"E23.1.0.0"),sQuery(id+"F0.wireOp",EDGE,"E23.1.0.1"),sQuery(id+"F0.wireOp",EDGE,"E23.1.0.2"),sQuery(id+"F0.wireOp",EDGE,"E23.2.0.0"),sQuery(id+"F0.wireOp",EDGE,"E23.2.0.1"),sQuery(id+"F0.wireOp",EDGE,"E23.2.0.2"),sQuery(id+"F0.wireOp",EDGE,"E23.3.0.0"),sQuery(id+"F0.wireOp",EDGE,"E23.3.0.1"),sQuery(id+"F0.wireOp",EDGE,"E23.3.0.2"),sQuery(id+"F0.wireOp",EDGE,"E23.4.0.0"),sQuery(id+"F0.wireOp",EDGE,"E23.4.0.1"),sQuery(id+"F0.wireOp",EDGE,"E23.4.0.2"),sQuery(id+"F0.wireOp",EDGE,"E23.5.0.0"),sQuery(id+"F0.wireOp",EDGE,"E23.5.0.1"),sQuery(id+"F0.wireOp",EDGE,"E23.5.0.2"),sQuery(id+"F0.wireOp",EDGE,"E24"),sQuery(id+"F0.wireOp",EDGE,"E25"),sQuery(id+"F0.wireOp",EDGE,"E26"),sQuery(id+"F0.wireOp",EDGE,"E27"),sQuery(id+"F0.wireOp",EDGE,"E28.0"),sQuery(id+"F0.wireOp",EDGE,"E28.1"),sQuery(id+"F0.wireOp",EDGE,"E28.2"),sQuery(id+"F0.wireOp",EDGE,"E28.3"),sQuery(id+"F0.wireOp",EDGE,"E29"),sQuery(id+"F0.wireOp",EDGE,"E30"),sQuery(id+"F0.wireOp",EDGE,"E31"),sQuery(id+"F0.wireOp",EDGE,"E32"),sQuery(id+"F0.wireOp",EDGE,"E33.0"),sQuery(id+"F0.wireOp",EDGE,"E33.1"),sQuery(id+"F0.wireOp",EDGE,"E33.2"),sQuery(id+"F0.wireOp",EDGE,"E33.3"),sQuery(id+"F0.wireOp",EDGE,"E34"),sQuery(id+"F0.wireOp",EDGE,"E35"),sQuery(id+"F0.wireOp",EDGE,"E36.trimOffspring"),sQuery(id+"F0.wireOp",EDGE,"E37.trimOffspring"),sQuery(id+"F0.wireOp",EDGE,"E38.trimOffspring"),sQuery(id+"F0.wireOp",EDGE,"E39.trimOffspring"),sQuery(id+"F0.wireOp",EDGE,"E40"),sQuery(id+"F0.wireOp",EDGE,"E41"),sQuery(id+"F0.wireOp",EDGE,"E42"),sQuery(id+"F0.wireOp",EDGE,"E43"),sQuery(id+"F0.wireOp",EDGE,"E44.trimOffspring"),sQuery(id+"F0.wireOp",EDGE,"E45.trimOffspring"),sQuery(id+"F0.wireOp",EDGE,"E46"),sQuery(id+"F0.wireOp",EDGE,"E47"),sQuery(id+"F0.wireOp",EDGE,"E48"),sQuery(id+"F0.wireOp",EDGE,"E49"),sQuery(id+"F0.wireOp",EDGE,"E50.0"),sQuery(id+"F0.wireOp",EDGE,"E50.1"),sQuery(id+"F0.wireOp",EDGE,"E50.2"),sQuery(id+"F0.wireOp",EDGE,"E50.3"),sQuery(id+"F0.wireOp",EDGE,"E51"),sQuery(id+"F0.wireOp",EDGE,"E52"),sQuery(id+"F0.wireOp",EDGE,"E53"),sQuery(id+"F0.wireOp",EDGE,"E54"),sQuery(id+"F0.wireOp",EDGE,"E55.0"),sQuery(id+"F0.wireOp",EDGE,"E55.1"),sQuery(id+"F0.wireOp",EDGE,"E55.2"),sQuery(id+"F0.wireOp",EDGE,"E55.3"),sQuery(id+"F0.wireOp",EDGE,"E56"),sQuery(id+"F0.wireOp",EDGE,"E57"),sQuery(id+"F0.wireOp",EDGE,"E58.trimOffspring"),sQuery(id+"F0.wireOp",EDGE,"E59.trimOffspring"),sQuery(id+"F0.wireOp",EDGE,"E60.trimOffspring"),sQuery(id+"F0.wireOp",EDGE,"E61.trimOffspring"),sQuery(id+"F0.wireOp",EDGE,"E62"),sQuery(id+"F0.wireOp",EDGE,"E63"),sQuery(id+"F0.wireOp",EDGE,"E64"),sQuery(id+"F0.wireOp",EDGE,"E65"),sQuery(id+"F0.wireOp",EDGE,"E66.trimOffspring"),sQuery(id+"F0.wireOp",EDGE,"E67.trimOffspring"),sQuery(id+"F0.wireOp",EDGE,"E68"),sQuery(id+"F0.wireOp",EDGE,"E69"),sQuery(id+"F0.wireOp",EDGE,"E70"),sQuery(id+"F0.wireOp",EDGE,"E71"),sQuery(id+"F0.wireOp",EDGE,"E72.0"),sQuery(id+"F0.wireOp",EDGE,"E72.1"),sQuery(id+"F0.wireOp",EDGE,"E72.2"),sQuery(id+"F0.wireOp",EDGE,"E72.3"),sQuery(id+"F0.wireOp",EDGE,"E73"),sQuery(id+"F0.wireOp",EDGE,"E74"),sQuery(id+"F0.wireOp",EDGE,"E75"),sQuery(id+"F0.wireOp",EDGE,"E76"),sQuery(id+"F0.wireOp",EDGE,"E77.0"),sQuery(id+"F0.wireOp",EDGE,"E77.1"),sQuery(id+"F0.wireOp",EDGE,"E77.2"),sQuery(id+"F0.wireOp",EDGE,"E77.3"),sQuery(id+"F0.wireOp",EDGE,"E78"),sQuery(id+"F0.wireOp",EDGE,"E79"),sQuery(id+"F0.wireOp",EDGE,"E80.trimOffspring"),sQuery(id+"F0.wireOp",EDGE,"E81.trimOffspring"),sQuery(id+"F0.wireOp",EDGE,"E82.trimOffspring"),sQuery(id+"F0.wireOp",EDGE,"E83.trimOffspring"),sQuery(id+"F0.wireOp",EDGE,"E84"),sQuery(id+"F0.wireOp",EDGE,"E85"),sQuery(id+"F0.wireOp",EDGE,"E86"),sQuery(id+"F0.wireOp",EDGE,"E87"),sQuery(id+"F0.wireOp",EDGE,"E88.trimOffspring"),sQuery(id+"F0.wireOp",EDGE,"E89.trimOffspring"),sQuery(id+"F0.wireOp",EDGE,"E90"),sQuery(id+"F0.wireOp",EDGE,"E91"),sQuery(id+"F0.wireOp",EDGE,"E92"),sQuery(id+"F0.wireOp",EDGE,"E93"),sQuery(id+"F0.wireOp",EDGE,"E94"),sQuery(id+"F0.wireOp",EDGE,"E95"),sQuery(id+"F0.wireOp",EDGE,"E96.1.0.0"),sQuery(id+"F0.wireOp",EDGE,"E96.1.0.1"),sQuery(id+"F0.wireOp",EDGE,"E96.1.0.2"),sQuery(id+"F0.wireOp",EDGE,"E96.2.0.0"),sQuery(id+"F0.wireOp",EDGE,"E96.2.0.1"),sQuery(id+"F0.wireOp",EDGE,"E96.2.0.2"),sQuery(id+"F0.wireOp",EDGE,"E96.3.0.0"),sQuery(id+"F0.wireOp",EDGE,"E96.3.0.1"),sQuery(id+"F0.wireOp",EDGE,"E96.3.0.2"),sQuery(id+"F0.wireOp",EDGE,"E96.4.0.0"),sQuery(id+"F0.wireOp",EDGE,"E96.4.0.1"),sQuery(id+"F0.wireOp",EDGE,"E96.4.0.2"),sQuery(id+"F0.wireOp",EDGE,"E96.5.0.0"),sQuery(id+"F0.wireOp",EDGE,"E96.5.0.1"),sQuery(id+"F0.wireOp",EDGE,"E96.5.0.2"),sQuery(id+"F0.wireOp",EDGE,"E97.1.0.0"),sQuery(id+"F0.wireOp",EDGE,"E97.1.0.1"),sQuery(id+"F0.wireOp",EDGE,"E97.1.0.2"),sQuery(id+"F0.wireOp",EDGE,"E97.2.0.0"),sQuery(id+"F0.wireOp",EDGE,"E97.2.0.1"),sQuery(id+"F0.wireOp",EDGE,"E97.2.0.2"),sQuery(id+"F0.wireOp",EDGE,"E97.3.0.0"),sQuery(id+"F0.wireOp",EDGE,"E97.3.0.1"),sQuery(id+"F0.wireOp",EDGE,"E97.3.0.2"),sQuery(id+"F0.wireOp",EDGE,"E97.4.0.0"),sQuery(id+"F0.wireOp",EDGE,"E97.4.0.1"),sQuery(id+"F0.wireOp",EDGE,"E97.4.0.2"),sQuery(id+"F0.wireOp",EDGE,"E97.5.0.0"),sQuery(id+"F0.wireOp",EDGE,"E97.5.0.1"),sQuery(id+"F0.wireOp",EDGE,"E97.5.0.2"),sQuery(id+"F0.wireOp",EDGE,"E98.trimOffspring"),sQuery(id+"F0.wireOp",EDGE,"E99.trimOffspring"),sQuery(id+"F0.wireOp",EDGE,"E100.trimOffspring"),sQuery(id+"F0.wireOp",EDGE,"E101.trimOffspring"),sQuery(id+"F0.wireOp",EDGE,"E102.trimOffspring"),sQuery(id+"F0.wireOp",EDGE,"E103.trimOffspring"),sQuery(id+"F0.wireOp",EDGE,"E104.trimOffspring"),sQuery(id+"F0.wireOp",EDGE,"E105.trimOffspring"),sQuery(id+"F0.wireOp",EDGE,"E106.trimOffspring"),sQuery(id+"F0.wireOp",EDGE,"E107.trimOffspring"),sQuery(id+"F0.wireOp",EDGE,"E108.trimOffspring"),sQuery(id+"F0.wireOp",EDGE,"E109.trimOffspring"),sQuery(id+"F0.wireOp",EDGE,"E110"),sQuery(id+"F0.wireOp",EDGE,"E111"),sQuery(id+"F0.wireOp",EDGE,"E112"),sQuery(id+"F0.wireOp",EDGE,"E113.1.0.0"),sQuery(id+"F0.wireOp",EDGE,"E113.1.0.1"),sQuery(id+"F0.wireOp",EDGE,"E113.1.0.2"),sQuery(id+"F0.wireOp",EDGE,"E113.2.0.0"),sQuery(id+"F0.wireOp",EDGE,"E113.2.0.1"),sQuery(id+"F0.wireOp",EDGE,"E113.2.0.2"),sQuery(id+"F0.wireOp",EDGE,"E113.3.0.0"),sQuery(id+"F0.wireOp",EDGE,"E113.3.0.1"),sQuery(id+"F0.wireOp",EDGE,"E113.3.0.2"),sQuery(id+"F0.wireOp",EDGE,"E113.4.0.0"),sQuery(id+"F0.wireOp",EDGE,"E113.4.0.1"),sQuery(id+"F0.wireOp",EDGE,"E113.4.0.2"),sQuery(id+"F0.wireOp",EDGE,"E113.5.0.0"),sQuery(id+"F0.wireOp",EDGE,"E113.5.0.1"),sQuery(id+"F0.wireOp",EDGE,"E113.5.0.2"),sQuery(id+"F0.wireOp",EDGE,"E114.trimOffspring"),sQuery(id+"F0.wireOp",EDGE,"E115.trimOffspring"),sQuery(id+"F0.wireOp",EDGE,"E116.trimOffspring"),sQuery(id+"F0.wireOp",EDGE,"E117.trimOffspring"),sQuery(id+"F0.wireOp",EDGE,"E118.trimOffspring"),sQuery(id+"F0.wireOp",EDGE,"E119.trimOffspring")])],"isStart":false});
            cPlane(context, id + "F2", {"entities" : qUnion([Q0]), "cplaneType" : CPlaneType.OFFSET, "offset" : 5 * mm, "width" : 150 * mm, "height" : 150 * mm});
        }
        {
            var Q0;
            Q0=qCreatedBy(id+"F2.planeOp",FACE);
            var sketch = newSketch(context, id + "F3", { "sketchPlane" : qUnion([Q0])});
            skLineSegment(sketch, "E125", {"start": v(0, -42.5) * mm, "end": v(58.74, -42.5) * mm});
            skLineSegment(sketch, "E126", {"start": v(58.74, -42.5) * mm, "end": v(58.74, -102.1) * mm});
            skLineSegment(sketch, "E127", {"start": v(58.74, -102.1) * mm, "end": v(0, -102.1) * mm});
            skLineSegment(sketch, "E128", {"start": v(0, -102.1) * mm, "end": v(0, -42.5) * mm});
            skSolve(sketch);
        }
        {
            var Q0;
            Q0=makeQuery(id+"F3.imprint","IMPRINT",FACE,{"disambiguationData":[TD([[makeQuery(id+"F3.imprint","IMPRINT",EDGE,{"derivedFrom":sQuery(id+"F3.wireOp",EDGE,"E125")}),-1.0]])]});
            extrude(context, id + "F4", {"entities" : qUnion([Q0]), "oppositeDirection" : true, "depth" : 2 * mm});
        }
        {
            var Q0;
            Q0=qCreatedBy(makeId("Right.planeOp"),FACE);
            cPlane(context, id + "F5", {"entities" : qUnion([Q0]), "cplaneType" : CPlaneType.OFFSET, "offset" : 30 * mm, "width" : 150 * mm, "height" : 150 * mm});
        }
        {
            var Q0;
            Q0=qCreatedBy(id+"F5.planeOp",FACE);
            var sketch = newSketch(context, id + "F6", { "sketchPlane" : qUnion([Q0])});
            skLineSegment(sketch, "E129", {"start": v(50.03, 1.02) * mm, "end": v(-42.5, 4) * mm});
            skLineSegment(sketch, "E130", {"start": v(-42.5, 4) * mm, "end": v(-42.5, 6) * mm});
            skLineSegment(sketch, "E131", {"start": v(-42.5, 6) * mm, "end": v(50.03, 3.08) * mm});
            skLineSegment(sketch, "E132", {"start": v(-102.1, 6) * mm, "end": v(-102.1, 4) * mm});
            skLineSegment(sketch, "E133", {"start": v(50.03, 1.02) * mm, "end": v(60.03, 1.02) * mm});
            skLineSegment(sketch, "E134", {"start": v(60.03, 1.02) * mm, "end": v(60.03, 3.08) * mm});
            skLineSegment(sketch, "E135", {"start": v(60.03, 3.08) * mm, "end": v(50.03, 3.08) * mm});
            skLineSegment(sketch, "E136", {"start": v(-204.87, 1) * mm, "end": v(-204.87, 3) * mm});
            skLineSegment(sketch, "E137", {"start": v(-204.87, 3) * mm, "end": v(-195.07, 3) * mm});
            skLineSegment(sketch, "E138", {"start": v(-195.07, 3) * mm, "end": v(-102.1, 6) * mm});
            skLineSegment(sketch, "E139", {"start": v(-102.1, 4) * mm, "end": v(-195.07, 1) * mm});
            skLineSegment(sketch, "E140", {"start": v(-195.07, 1) * mm, "end": v(-204.87, 1) * mm});
            skSolve(sketch);
        }
        {
            var Q0;
            Q0=qSketchRegion(id+"F6",true);
            extrude(context, id + "F7", {"entities" : qUnion([Q0]), "endBound" : BoundingType.SYMMETRIC, "depth" : 10 * mm});
        }
    });
